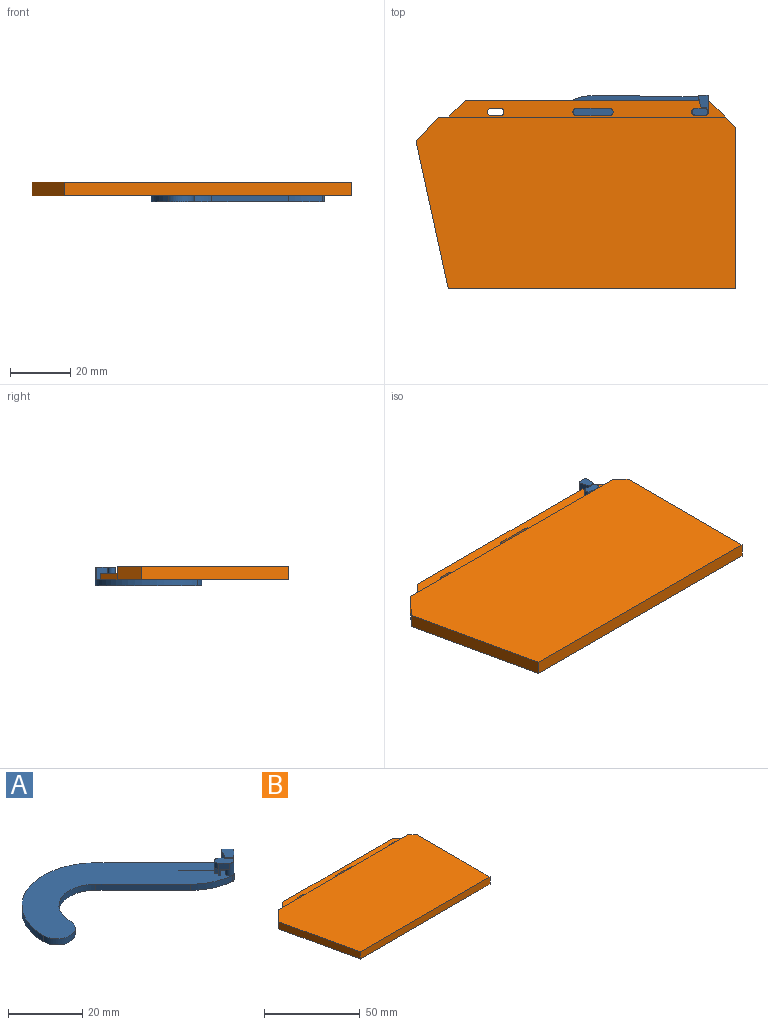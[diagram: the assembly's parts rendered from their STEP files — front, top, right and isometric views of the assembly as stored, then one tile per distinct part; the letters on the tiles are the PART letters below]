
ASSEMBLY  parts=2 mates=1
PART A: 35 faces, bbox 60.7x36.1x6.2 mm
  f0: plane 1.8x1.62mm, normal (-0.71,-0.71,0), area 4.1mm2, adj f2,f22,f23,f33
  f1: plane 4.21x2.1mm, normal (0.72,0.69,0), area 6.5mm2, adj f3,f4,f19,f20,f25,f26,f28,f33
  f2: plane 6.21x3.62mm, normal (0.71,-0.71,0), area 17.1mm2, adj f0,f4,f9,f10,f18,f20,f22,f24
  f3: cylinder r=1.2mm len=4.21mm, axis (0,0,-1), area 8.4mm2, adj f1,f4,f19,f21,f27,f29,f30,f31
  f4: plane 59.72x36.1mm, normal (0,0,1), area 734.7mm2, adj f1,f2,f3,f5,f6,f7,f8,f9
  f5: cylinder r=17.65mm len=10.86mm, axis (0,0,1), area 24.5mm2, adj f4,f6,f17,f18
  f6: cylinder r=1.26mm len=2.15mm, axis (0,0,1), area 6.2mm2, adj f4,f5,f7,f18
  f7: plane 9.63x9.63mm, normal (0.71,0.71,0), area 27.2mm2, adj f4,f6,f8,f18
  f8: cylinder r=0.15mm len=2mm, axis (0,0,1), area 0.9mm2, adj f4,f7,f9,f18
  f9: plane 10.5x10.5mm, normal (-0.71,-0.71,0), area 29.7mm2, adj f2,f4,f8,f18
  f10: cylinder r=0.39mm len=6.21mm, axis (0,0,1), area 3.8mm2, adj f2,f11,f18,f22
  f11: plane 6.21x1.84mm, normal (0.71,0.71,0), area 16.1mm2, adj f10,f12,f18,f22
  f12: cylinder r=0.39mm len=6.21mm, axis (0,0,1), area 4.5mm2, adj f11,f13,f18,f22,f23
  f13: plane 23.98x23.98mm, normal (0.71,0.71,0), area 67.8mm2, adj f4,f12,f14,f18
  f14: cylinder r=20mm len=34.14mm, axis (0,0,1), area 94.2mm2, adj f4,f13,f15,f18
  f15: cylinder r=5mm len=10mm, axis (0,0,1), area 31.4mm2, adj f4,f14,f16,f18
  f16: cylinder r=10mm len=17.07mm, axis (0,0,1), area 47.1mm2, adj f4,f15,f17,f18
  f17: plane 18.07x18.07mm, normal (-0.71,-0.71,0), area 51.1mm2, adj f4,f5,f16,f18
  f18: plane 60.69x36.1mm, normal (0,0,-1), area 745.8mm2, adj f2,f5,f6,f7,f8,f9,f10,f11
  f19: plane 4.5x4.42mm, normal (0,0,1), area 11.5mm2, adj f1,f3,f20,f21
  f20: cylinder r=1.2mm len=4.21mm, axis (0,0,-1), area 23.8mm2, adj f1,f2,f4,f19,f21,f25,f33
  f21: plane 4.21x2.1mm, normal (-0.72,-0.69,0), area 6.7mm2, adj f3,f4,f19,f20,f25,f26,f32
  f22: plane 4.98x4.21mm, normal (0,0,1), area 11.2mm2, adj f0,f2,f10,f11,f12,f23
  f23: plane 4.21x3.16mm, normal (-0.89,0.46,0), area 9.7mm2, adj f0,f4,f12,f22,f24,f25,f34
  f24: plane 2.21x2.13mm, normal (-0.71,-0.71,0), area 6.6mm2, adj f2,f4,f23,f25
  f25: plane 6.21x4.89mm, normal (0,0,-1), area 11.1mm2, adj f1,f2,f20,f21,f23,f24,f26,f34
  f26: plane 2.21x1.73mm, normal (0.69,-0.72,0), area 5.3mm2, adj f1,f4,f21,f25
  f27: plane 1.54x1.06mm, normal (0,0,-1), area 0.9mm2, adj f3,f28,f29
  f28: plane 2.21x0.72mm, normal (-0.69,0.72,0), area 2.2mm2, adj f1,f4,f27,f29
  f29: plane 2.21x0.85mm, normal (0.72,0.69,0), area 2.6mm2, adj f3,f4,f27,f28
  f30: plane 1.55x1.06mm, normal (0,0,-1), area 0.9mm2, adj f3,f31,f32
  f31: plane 2.21x0.85mm, normal (-0.72,-0.69,0), area 2.6mm2, adj f3,f4,f30,f32
  f32: plane 2.21x0.72mm, normal (-0.69,0.72,0), area 2.2mm2, adj f4,f21,f30,f31
  f33: plane 2.75x1.9mm, normal (0,0,1), area 1.2mm2, adj f0,f1,f2,f20,f34
  f34: plane 0.29x0.25mm, normal (-0.65,0.76,0), area 0.1mm2, adj f1,f23,f25,f33
PART B: 23 faces, bbox 106.5x62.7x4.6 mm
  f0: plane 9.11x9.11mm, normal (0.71,0.71,0), area 40.2mm2, adj f1,f5,f6,f7,f11,f22
  f1: plane 95.68x4.55mm, normal (0,1,0), area 231.7mm2, adj f0,f2,f6,f7,f12,f22
  f2: plane 8.04x7.33mm, normal (-0.74,0.67,0), area 49.5mm2, adj f1,f3,f6,f7
  f3: plane 49.12x10.72mm, normal (-0.98,-0.21,0), area 228.8mm2, adj f2,f4,f6,f7
  f4: plane 95.82x4.55mm, normal (0,-1,0), area 436mm2, adj f3,f5,f6,f7
  f5: plane 53.63x4.55mm, normal (1,0,0), area 244mm2, adj f0,f4,f6,f7
  f6: plane 106.54x57.16mm, normal (0,0,1), area 5791mm2, adj f0,f1,f2,f3,f4,f5
  f7: plane 106.54x62.74mm, normal (0,0,-1), area 6215.1mm2, adj f0,f1,f2,f3,f4,f5,f8,f9
  f8: cylinder r=1.3mm len=2.6mm, axis (0,0,-1), area 9mm2, adj f7,f9,f21,f22
  f9: plane 2.91x2.21mm, normal (0,-1,0), area 6.4mm2, adj f7,f8,f10,f22
  f10: cylinder r=1.3mm len=2.6mm, axis (0,0,-1), area 9mm2, adj f7,f9,f21,f22
  f11: plane 81x2.21mm, normal (0,1,0), area 179mm2, adj f0,f7,f12,f22
  f12: plane 5.58x5.58mm, normal (-0.71,0.71,0), area 17.4mm2, adj f1,f7,f11,f22
  f13: plane 10.8x2.21mm, normal (0,1,0), area 23.9mm2, adj f7,f14,f19,f22
  f14: cylinder r=1.3mm len=2.6mm, axis (0,0,-1), area 9mm2, adj f7,f13,f15,f22
  f15: plane 10.8x2.21mm, normal (0,-1,0), area 23.9mm2, adj f7,f14,f19,f22
  f16: plane 2.88x2.21mm, normal (0,1,0), area 6.4mm2, adj f7,f17,f20,f22
  f17: cylinder r=1.3mm len=2.6mm, axis (0,0,-1), area 9mm2, adj f7,f16,f18,f22
  f18: plane 2.88x2.21mm, normal (0,-1,0), area 6.4mm2, adj f7,f17,f20,f22
  f19: cylinder r=1.3mm len=2.6mm, axis (0,0,-1), area 9mm2, adj f7,f13,f15,f22
  f20: cylinder r=1.3mm len=2.6mm, axis (0,0,-1), area 9mm2, adj f7,f16,f18,f22
  f21: plane 2.91x2.21mm, normal (0,1,0), area 6.4mm2, adj f7,f8,f10,f22
  f22: plane 92.16x5.58mm, normal (0,0,1), area 424.1mm2, adj f0,f1,f8,f9,f10,f11,f12,f13
PLACE A rot(axis=(0,0,1),44.1deg) t=(30.82,-16.79,0)mm
PLACE B at identity fixed
MATE revolute A.f20 <-> B.f10  axis (0,0,1) through (36.11,29.61,0)mm
